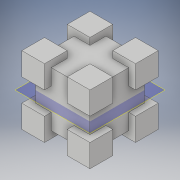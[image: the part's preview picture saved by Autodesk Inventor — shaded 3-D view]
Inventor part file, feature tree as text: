
AUTODESK INVENTOR PART (.ipt)
format: ipt  version: 2018 (Build 220112000, 112)  size: 221,184 bytes
history: native  units: in
note: dims shown in document units (in); Inventor stores cm internally (conversion verified against a paired STEP export)
features: extrude x4, plane x4, sketch x4, mirror x3
ambient origin geometry x8: Origin, YZ Plane, XZ Plane, XY Plane, X Axis, Y Axis, Z Axis, Center Point
bodies: Solid1 (feature_tree)
feature tree (15):
  extrude  "Extrusion1"  Depth=1.0in
  extrude  "Extrusion2"  Depth=0.333in
  extrude  "Extrusion3"  Depth=0.333in
  extrude  "Extrusion4"  Depth=0.333in
  plane  "Work Plane1"
  plane  "Work Plane2"
  plane  "Work Plane3"
  mirror  "Mirror1"
  mirror  "Mirror2"
  mirror  "Mirror3"
  sketch  "Sketch1"  dims[d0=1.0in d1=1.0in]
  sketch  "Sketch3"  dims[d2=1.0in d3=0.0in d4=0.333in]
  sketch  "Sketch5"  dims[d5=0.333in d6=0.333in]
  sketch  "Sketch7"  dims[d7=0.333in d8=0.333in d9=0.333in d10=0.333in d11=0.333in d12=0.1in d13=0.0in d14=0.333in d15=0.333in d16=0.333in d17=0.333in d18=0.333in d19=0.333in d20=0.333in d21=0.333in d22=0.1in d23=0.0in d32=0.333in d33=0.333in d34=0.333in d35=0.333in d36=0.333in d37=0.333in d38=0.333in d39=0.333in d40=0.1in d41=0.0in d42=0.5in d43=0.5in]
  plane  "Work Plane4"
